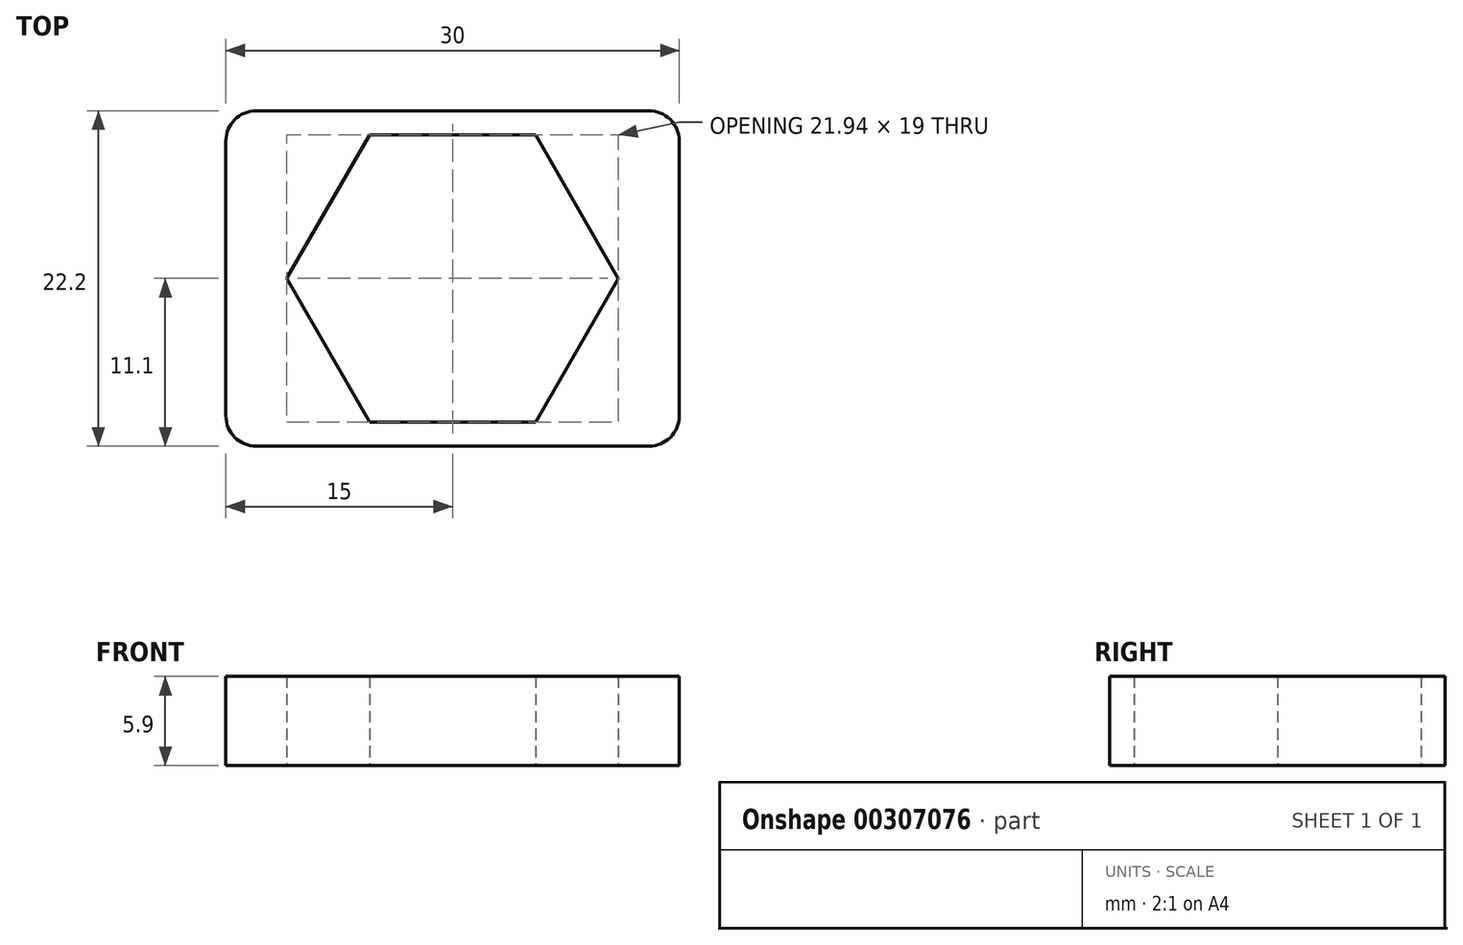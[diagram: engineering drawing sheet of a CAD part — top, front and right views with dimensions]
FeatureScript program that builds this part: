
annotation { "Feature Type Name" : "Feature", "Feature Type Description" : "" }
export const myFeature = defineFeature(function(context is Context, id is Id, definition is map)
    precondition{}
    {
        {
            var Q0;
            Q0=qCreatedBy(makeId("Top.planeOp"),FACE);
            var sketch = newSketch(context, id + "F0", { "sketchPlane" : qUnion([Q0])});
            skCircle(sketch, "E0.cCircle", {"center": v(0, 0) * mm, "radius": 9.5 * mm, "construction": true});
            skLineSegment(sketch, "E0.0", {"start": v(5.49, 9.5) * mm, "end": v(10.97, 0) * mm});
            skLineSegment(sketch, "E0.1", {"start": v(10.97, 0) * mm, "end": v(5.48, -9.5) * mm});
            skLineSegment(sketch, "E0.2", {"start": v(5.48, -9.5) * mm, "end": v(-5.49, -9.5) * mm});
            skLineSegment(sketch, "E0.3", {"start": v(-5.49, -9.5) * mm, "end": v(-10.97, 0) * mm});
            skLineSegment(sketch, "E0.4", {"start": v(-10.97, 0) * mm, "end": v(-5.48, 9.5) * mm});
            skLineSegment(sketch, "E0.5", {"start": v(-5.48, 9.5) * mm, "end": v(5.49, 9.5) * mm});
            skPoint(sketch, "E0.0.midPoint", {"position": v(8.23, 4.75) * mm});
            skLineSegment(sketch, "E1.bottom", {"start": v(-15, 11.1) * mm, "end": v(15, 11.1) * mm});
            skLineSegment(sketch, "E1.top", {"start": v(-15, -11.1) * mm, "end": v(15, -11.1) * mm});
            skLineSegment(sketch, "E1.left", {"start": v(-15, 11.1) * mm, "end": v(-15, -11.1) * mm});
            skLineSegment(sketch, "E1.right", {"start": v(15, 11.1) * mm, "end": v(15, -11.1) * mm});
            skSolve(sketch);
        }
        {
            var Q0;
            Q0 = qSketchRegion(id + "F0", true);
            extrude(context, id + "F1", {"entities" : qUnion([Q0]), "depth" : 5.9 * mm});
        }
        {
            var Q0;
            Q0=makeQuery(id+"F1.opExtrude","SWEPT_EDGE",EDGE,{"disambiguationData":[OSD([sQuery(id+"F0.wireOp",EDGE,"E1.bottom"),sQuery(id+"F0.wireOp",EDGE,"E1.right")])]});
            var Q1;
            Q1=makeQuery(id+"F1.opExtrude","SWEPT_EDGE",EDGE,{"disambiguationData":[OSD([sQuery(id+"F0.wireOp",EDGE,"E1.top"),sQuery(id+"F0.wireOp",EDGE,"E1.right")])]});
            var Q2;
            Q2=makeQuery(id+"F1.opExtrude","SWEPT_EDGE",EDGE,{"disambiguationData":[OSD([sQuery(id+"F0.wireOp",EDGE,"E1.bottom"),sQuery(id+"F0.wireOp",EDGE,"E1.left")])]});
            var Q3;
            Q3=makeQuery(id+"F1.opExtrude","SWEPT_EDGE",EDGE,{"disambiguationData":[OSD([sQuery(id+"F0.wireOp",EDGE,"E1.top"),sQuery(id+"F0.wireOp",EDGE,"E1.left")])]});
            fillet(context, id + "F2", {"entities" : qUnion([Q0, Q1, Q2, Q3]), "radius" : 2 * mm, "tangentPropagation" : true, "allowEdgeOverflow" : false});
        }
    });
